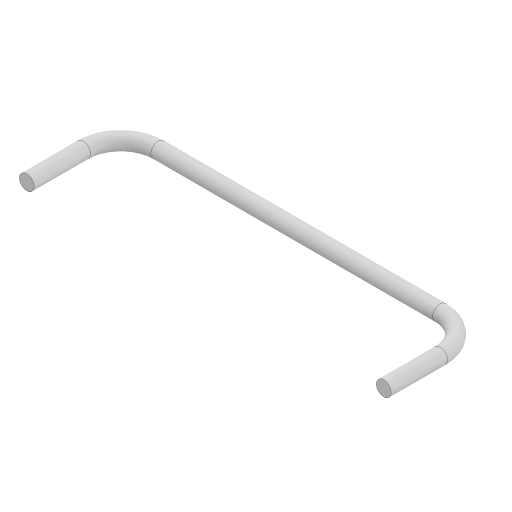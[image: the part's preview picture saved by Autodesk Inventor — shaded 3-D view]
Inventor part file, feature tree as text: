
AUTODESK INVENTOR PART (.ipt)
format: ipt  version: 2024.3 (Build 283343000, 343)  size: 112,128 bytes
history: native  units: mm
features: sketch x3, extrude x2, mirror x2, revolve x1, projected_geometry x1
ambient origin geometry x8: Origin, YZ Plane, XZ Plane, XY Plane, X Axis, Y Axis, Z Axis, Center Point
bodies: Solid1 (feature_tree)
feature tree (9):
  extrude  "Extrusion1"  Depth=150.0mm TaperAngle=0.0deg
  revolve  "Revolution1"  [1 undecoded]
  mirror  "Mirror1"
  extrude  "Extrusion3"  Depth=30.0mm TaperAngle=0.0deg
  mirror  "Mirror2"
  sketch  "Sketch1"  dims[d0=8.0mm d1=150.0mm d2=0.0mm]
  sketch  "Sketch4"  dims[d9=90.0deg d10=20.0mm]
  sketch  "Sketch5"  dims[d11=0.0mm d12=30.0mm d13=0.0mm d7=0.5mm d8=0.872665mm]
  projected_geometry  "Projected Loop2"
note: 1 required parameter value undecoded (feature->parameter linkage not recoverable at this tier; creation-order binding heuristic only, values carry confidence <= 0.55)
